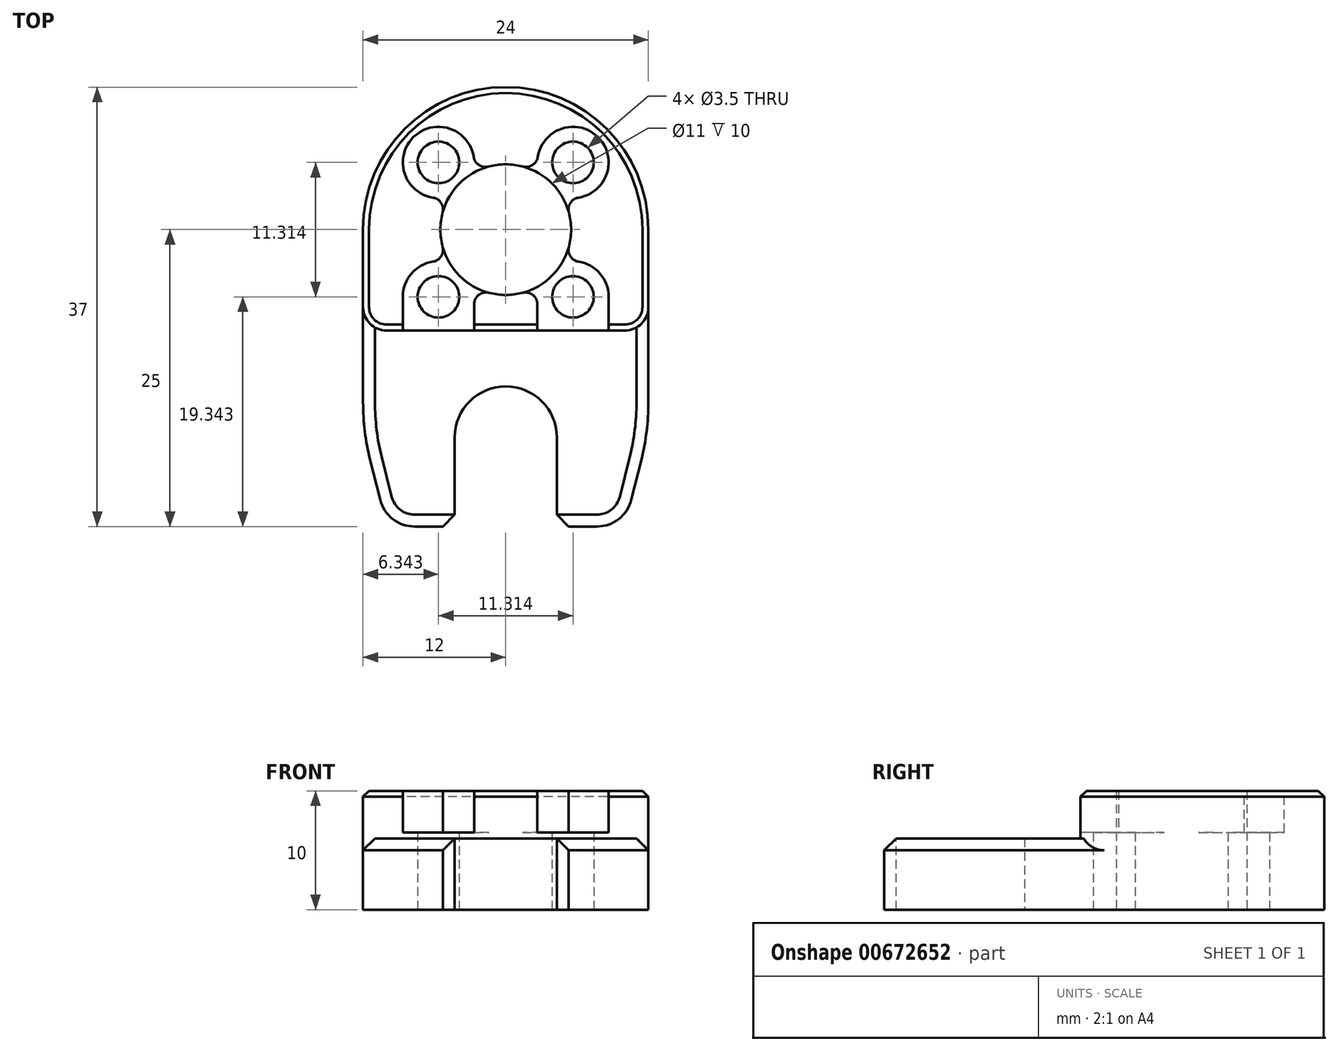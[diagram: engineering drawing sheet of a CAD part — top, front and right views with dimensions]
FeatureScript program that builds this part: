
annotation { "Feature Type Name" : "Feature", "Feature Type Description" : "" }
export const myFeature = defineFeature(function(context is Context, id is Id, definition is map)
    precondition{}
    {
        {
            var Q0;
            Q0=qCreatedBy(makeId("Top.planeOp"),FACE);
            var sketch = newSketch(context, id + "F0", { "sketchPlane" : qUnion([Q0])});
            skCircle(sketch, "E0", {"center": v(0, 0) * mm, "radius": 5.5 * mm});
            skLineSegment(sketch, "E1", {"start": v(0, 0) * mm, "end": v(0, 8) * mm, "construction": true});
            skCircle(sketch, "E2", {"center": v(0, 8) * mm, "radius": 1.75 * mm});
            skCircle(sketch, "E3.1.0", {"center": v(-8, 0) * mm, "radius": 1.75 * mm});
            skCircle(sketch, "E3.2.0", {"center": v(0, -8) * mm, "radius": 1.75 * mm});
            skCircle(sketch, "E3.3.0", {"center": v(8, 0) * mm, "radius": 1.75 * mm});
            skLineSegment(sketch, "E4", {"start": v(0, 0) * mm, "end": v(8, 0) * mm, "construction": true});
            skArc(sketch, "E5", {"start": v(8.49, -8.49) * mm, "mid": v(8.49, 8.49) * mm, "end": v(-8.49, 8.49) * mm});
            skLineSegment(sketch, "E6", {"start": v(0, 0) * mm, "end": v(-17.68, -17.68) * mm, "construction": true});
            skLineSegment(sketch, "E7", {"start": v(-17.68, -17.68) * mm, "end": v(-12.37, -12.37) * mm, "construction": true});
            skArc(sketch, "E8.0.startCap", {"start": v(-14.64, -20.72) * mm, "mid": v(-20.72, -20.72) * mm, "end": v(-20.72, -14.64) * mm, "construction": true});
            skArc(sketch, "E8.0.endCap", {"start": v(-15.41, -9.33) * mm, "mid": v(-9.33, -9.33) * mm, "end": v(-9.33, -15.41) * mm});
            skLineSegment(sketch, "E8.0.left", {"start": v(-20.72, -14.64) * mm, "end": v(-15.41, -9.33) * mm});
            skLineSegment(sketch, "E8.0.right", {"start": v(-14.64, -20.72) * mm, "end": v(-9.33, -15.41) * mm});
            skLineSegment(sketch, "E9", {"start": v(8.49, -8.49) * mm, "end": v(-9.2, -26.16) * mm});
            skLineSegment(sketch, "E10", {"start": v(-8.49, 8.49) * mm, "end": v(-26.16, -9.2) * mm});
            skLineSegment(sketch, "E11", {"start": v(-14.64, -20.72) * mm, "end": v(-9.2, -26.16) * mm});
            skLineSegment(sketch, "E12", {"start": v(-20.72, -14.64) * mm, "end": v(-26.16, -9.2) * mm});
            skSolve(sketch);
        }
        {
            var Q0;
            Q0 = qSketchRegion(id + "F0", true);
            extrude(context, id + "F1", {"entities" : qUnion([Q0]), "depth" : 10 * mm, "offsetDistance" : 25 * mm});
        }
        {
            var Q0;
            Q0=makeQuery(id+"F1.opExtrude","SWEPT_EDGE",EDGE,{"disambiguationData":[OSD([sQuery(id+"F0.wireOp",EDGE,"E10"),sQuery(id+"F0.wireOp",EDGE,"E12")])]});
            chamfer(context, id + "F2", {"entities" : qUnion([Q0]), "chamferType" : ChamferType.TWO_OFFSETS, "width1" : 2 * mm, "oppositeDirection" : false, "width2" : 8 * mm, "tangentPropagation" : true});
        }
        {
            var Q0;
            Q0=makeQuery(id+"F1.opExtrude","SWEPT_EDGE",EDGE,{"disambiguationData":[OSD([sQuery(id+"F0.wireOp",EDGE,"E9"),sQuery(id+"F0.wireOp",EDGE,"E11")])]});
            chamfer(context, id + "F3", {"entities" : qUnion([Q0]), "chamferType" : ChamferType.TWO_OFFSETS, "width1" : 8 * mm, "oppositeDirection" : false, "width2" : 2 * mm, "tangentPropagation" : true});
        }
        {
            var Q0;
            Q0=makeQuery(id+"F1.opExtrude","SWEPT_FACE",FACE,{"disambiguationData":[OSD([sQuery(id+"F0.wireOp",EDGE,"E8.0.left")])]});
            cPlane(context, id + "F4", {"entities" : qUnion([Q0]), "cplaneType" : CPlaneType.OFFSET, "offset" : 5.05 * mm, "width" : 150 * mm, "height" : 150 * mm});
        }
        {
            var Q0;
            Q0=qCreatedBy(id+"F4.planeOp",FACE);
            var sketch = newSketch(context, id + "F5", { "sketchPlane" : qUnion([Q0])});
            skLineSegment(sketch, "E13", {"start": v(0, 0) * mm, "end": v(-8.5, 0) * mm, "construction": true});
            skLineSegment(sketch, "E14", {"start": v(-8.5, 0) * mm, "end": v(-8.5, 6) * mm, "construction": true});
            skLineSegment(sketch, "E15.bottom", {"start": v(-8.5, 6) * mm, "end": v(-28.5, 6) * mm});
            skLineSegment(sketch, "E15.top", {"start": v(-8.5, 14) * mm, "end": v(-28.5, 14) * mm});
            skLineSegment(sketch, "E15.left", {"start": v(-8.5, 6) * mm, "end": v(-8.5, 14) * mm});
            skLineSegment(sketch, "E15.right", {"start": v(-28.5, 6) * mm, "end": v(-28.5, 14) * mm});
            skSolve(sketch);
        }
        {
            var Q0;
            Q0 = qSketchRegion(id + "F5", true);
            extrude(context, id + "F6", {"entities" : qUnion([Q0]), "operationType" : NewBodyOperationType.REMOVE, "endBound" : BoundingType.SYMMETRIC, "oppositeDirection" : true, "depth" : 30 * mm, "offsetDistance" : 25 * mm});
        }
        {
            var Q0;
            Q0=makeQuery(id+"F1.opExtrude","CAP_FACE",FACE,{"disambiguationData":[OSD([sQuery(id+"F0.wireOp",EDGE,"E0"),sQuery(id+"F0.wireOp",EDGE,"E2"),sQuery(id+"F0.wireOp",EDGE,"E3.1.0"),sQuery(id+"F0.wireOp",EDGE,"E3.2.0"),sQuery(id+"F0.wireOp",EDGE,"E3.3.0"),sQuery(id+"F0.wireOp",EDGE,"E5"),sQuery(id+"F0.wireOp",EDGE,"E8.0.endCap"),sQuery(id+"F0.wireOp",EDGE,"E8.0.left"),sQuery(id+"F0.wireOp",EDGE,"E8.0.right"),sQuery(id+"F0.wireOp",EDGE,"E9"),sQuery(id+"F0.wireOp",EDGE,"E10"),sQuery(id+"F0.wireOp",EDGE,"E11"),sQuery(id+"F0.wireOp",EDGE,"E12")])],"isStart":false});
            var sketch = newSketch(context, id + "F7", { "sketchPlane" : qUnion([Q0])});
            skArc(sketch, "E16", {"start": v(-5.88, -2.12) * mm, "mid": v(-5.88, 2.12) * mm, "end": v(-10.12, 2.12) * mm});
            skArc(sketch, "E17", {"start": v(2.12, -10.12) * mm, "mid": v(2.12, -5.88) * mm, "end": v(-2.12, -5.88) * mm});
            skCircle(sketch, "E18", {"center": v(8, 0) * mm, "radius": 3 * mm});
            skCircle(sketch, "E19", {"center": v(0, 8) * mm, "radius": 3 * mm});
            skLineSegment(sketch, "E20", {"start": v(-8, 0) * mm, "end": v(-10.01, -2.01) * mm, "construction": true});
            skLineSegment(sketch, "E21", {"start": v(0, -8) * mm, "end": v(-2.01, -10.01) * mm, "construction": true});
            skLineSegment(sketch, "E22.0", {"start": v(-10.12, 2.12) * mm, "end": v(-12.13, 0.11) * mm});
            skLineSegment(sketch, "E23.MirrorCS", {"start": v(-5.88, -2.12) * mm, "end": v(-7.89, -4.13) * mm});
            skLineSegment(sketch, "E24", {"start": v(-12.13, 0.11) * mm, "end": v(-7.89, -4.13) * mm});
            skLineSegment(sketch, "E25.0", {"start": v(-2.12, -5.88) * mm, "end": v(-4.13, -7.89) * mm});
            skLineSegment(sketch, "E26.MirrorCS", {"start": v(2.12, -10.12) * mm, "end": v(0.11, -12.13) * mm});
            skLineSegment(sketch, "E27", {"start": v(-4.13, -7.89) * mm, "end": v(0.11, -12.13) * mm});
            skSolve(sketch);
        }
        {
            var Q0;
            Q0 = qSketchRegion(id + "F7", true);
            extrude(context, id + "F8", {"entities" : qUnion([Q0]), "operationType" : NewBodyOperationType.REMOVE, "oppositeDirection" : true, "depth" : 3.5 * mm, "offsetDistance" : 25 * mm});
        }
        {
            var Q0;
            Q0=makeQuery(id+"F8.boolean.opBoolean","INTERSECT",EDGE,{"disambiguationData":[OD(0.0)],"derivedFrom":[makeQuery(id+"F1.opExtrude","SWEPT_FACE",FACE,{"disambiguationData":[OSD([sQuery(id+"F0.wireOp",EDGE,"E0")])]}),makeQuery(id+"F8.opExtrude","SWEPT_FACE",FACE,{"disambiguationData":[OSD([sQuery(id+"F7.wireOp",EDGE,"E16")])]})]});
            var Q1;
            Q1=makeQuery(id+"F8.boolean.opBoolean","INTERSECT",EDGE,{"disambiguationData":[OD(1.0)],"derivedFrom":[makeQuery(id+"F1.opExtrude","SWEPT_FACE",FACE,{"disambiguationData":[OSD([sQuery(id+"F0.wireOp",EDGE,"E0")])]}),makeQuery(id+"F8.opExtrude","SWEPT_FACE",FACE,{"disambiguationData":[OSD([sQuery(id+"F7.wireOp",EDGE,"E16")])]})]});
            var Q2;
            Q2=makeQuery(id+"F8.boolean.opBoolean","INTERSECT",EDGE,{"disambiguationData":[OD(0.0)],"derivedFrom":[makeQuery(id+"F1.opExtrude","SWEPT_FACE",FACE,{"disambiguationData":[OSD([sQuery(id+"F0.wireOp",EDGE,"E0")])]}),makeQuery(id+"F8.opExtrude","SWEPT_FACE",FACE,{"disambiguationData":[OSD([sQuery(id+"F7.wireOp",EDGE,"E17")])]})]});
            var Q3;
            Q3=makeQuery(id+"F8.boolean.opBoolean","INTERSECT",EDGE,{"disambiguationData":[OD(1.0)],"derivedFrom":[makeQuery(id+"F1.opExtrude","SWEPT_FACE",FACE,{"disambiguationData":[OSD([sQuery(id+"F0.wireOp",EDGE,"E0")])]}),makeQuery(id+"F8.opExtrude","SWEPT_FACE",FACE,{"disambiguationData":[OSD([sQuery(id+"F7.wireOp",EDGE,"E17")])]})]});
            var Q4;
            Q4=makeQuery(id+"F8.boolean.opBoolean","INTERSECT",EDGE,{"disambiguationData":[OD(0.0)],"derivedFrom":[makeQuery(id+"F1.opExtrude","SWEPT_FACE",FACE,{"disambiguationData":[OSD([sQuery(id+"F0.wireOp",EDGE,"E0")])]}),makeQuery(id+"F8.opExtrude","SWEPT_FACE",FACE,{"disambiguationData":[OSD([sQuery(id+"F7.wireOp",EDGE,"E18")])]})]});
            var Q5;
            Q5=makeQuery(id+"F8.boolean.opBoolean","INTERSECT",EDGE,{"disambiguationData":[OD(1.0)],"derivedFrom":[makeQuery(id+"F1.opExtrude","SWEPT_FACE",FACE,{"disambiguationData":[OSD([sQuery(id+"F0.wireOp",EDGE,"E0")])]}),makeQuery(id+"F8.opExtrude","SWEPT_FACE",FACE,{"disambiguationData":[OSD([sQuery(id+"F7.wireOp",EDGE,"E18")])]})]});
            var Q6;
            Q6=makeQuery(id+"F8.boolean.opBoolean","INTERSECT",EDGE,{"disambiguationData":[OD(1.0)],"derivedFrom":[makeQuery(id+"F1.opExtrude","SWEPT_FACE",FACE,{"disambiguationData":[OSD([sQuery(id+"F0.wireOp",EDGE,"E0")])]}),makeQuery(id+"F8.opExtrude","SWEPT_FACE",FACE,{"disambiguationData":[OSD([sQuery(id+"F7.wireOp",EDGE,"E19")])]})]});
            var Q7;
            Q7=makeQuery(id+"F8.boolean.opBoolean","INTERSECT",EDGE,{"disambiguationData":[OD(0.0)],"derivedFrom":[makeQuery(id+"F1.opExtrude","SWEPT_FACE",FACE,{"disambiguationData":[OSD([sQuery(id+"F0.wireOp",EDGE,"E0")])]}),makeQuery(id+"F8.opExtrude","SWEPT_FACE",FACE,{"disambiguationData":[OSD([sQuery(id+"F7.wireOp",EDGE,"E19")])]})]});
            fillet(context, id + "F9", {"entities" : qUnion([Q0, Q1, Q2, Q3, Q4, Q5, Q6, Q7]), "radius" : 1 * mm, "tangentPropagation" : true, "allowEdgeOverflow" : false});
        }
        {
            var Q0;
            Q0=makeQuery(id+"F6.boolean.opBoolean","INTERSECT",EDGE,{"derivedFrom":[makeQuery(id+"F1.opExtrude","SWEPT_FACE",FACE,{"disambiguationData":[OSD([sQuery(id+"F0.wireOp",EDGE,"E9")])]}),makeQuery(id+"F6.opExtrude","SWEPT_FACE",FACE,{"disambiguationData":[OSD([sQuery(id+"F5.wireOp",EDGE,"E15.left")])]})]});
            var Q1;
            Q1=makeQuery(id+"F6.boolean.opBoolean","INTERSECT",EDGE,{"derivedFrom":[makeQuery(id+"F1.opExtrude","SWEPT_FACE",FACE,{"disambiguationData":[OSD([sQuery(id+"F0.wireOp",EDGE,"E10")])]}),makeQuery(id+"F6.opExtrude","SWEPT_FACE",FACE,{"disambiguationData":[OSD([sQuery(id+"F5.wireOp",EDGE,"E15.left")])]})]});
            fillet(context, id + "F10", {"entities" : qUnion([Q0, Q1]), "radius" : 2 * mm, "tangentPropagation" : true, "allowEdgeOverflow" : false});
        }
        {
            var Q0;
            Q0=makeQuery(id+"F6.boolean.opBoolean","INTERSECT",EDGE,{"derivedFrom":[makeQuery(id+"F1.opExtrude","CAP_FACE",FACE,{"disambiguationData":[OSD([sQuery(id+"F0.wireOp",EDGE,"E0"),sQuery(id+"F0.wireOp",EDGE,"E2"),sQuery(id+"F0.wireOp",EDGE,"E3.1.0"),sQuery(id+"F0.wireOp",EDGE,"E3.2.0"),sQuery(id+"F0.wireOp",EDGE,"E3.3.0"),sQuery(id+"F0.wireOp",EDGE,"E5"),sQuery(id+"F0.wireOp",EDGE,"E8.0.endCap"),sQuery(id+"F0.wireOp",EDGE,"E8.0.left"),sQuery(id+"F0.wireOp",EDGE,"E8.0.right"),sQuery(id+"F0.wireOp",EDGE,"E9"),sQuery(id+"F0.wireOp",EDGE,"E10"),sQuery(id+"F0.wireOp",EDGE,"E11"),sQuery(id+"F0.wireOp",EDGE,"E12")])],"isStart":false}),makeQuery(id+"F6.opExtrude","SWEPT_FACE",FACE,{"disambiguationData":[OSD([sQuery(id+"F5.wireOp",EDGE,"E15.left")])]})]});
            var Q1;
            {var subQ0=sQuery(id+"F0.wireOp",EDGE,"E9");Q1=makeQuery(id+"F10.opFillet","BLEND_EDGE",EDGE,{"blendedFrom":[makeQuery(id+"F6.boolean.opBoolean","INTERSECT",EDGE,{"derivedFrom":[makeQuery(id+"F1.opExtrude","SWEPT_FACE",FACE,{"disambiguationData":[OSD([subQ0])]}),makeQuery(id+"F6.opExtrude","SWEPT_FACE",FACE,{"disambiguationData":[OSD([sQuery(id+"F5.wireOp",EDGE,"E15.left")])]})]}),makeQuery(id+"F1.opExtrude","CAP_FACE",FACE,{"disambiguationData":[OSD([sQuery(id+"F0.wireOp",EDGE,"E0"),sQuery(id+"F0.wireOp",EDGE,"E2"),sQuery(id+"F0.wireOp",EDGE,"E3.1.0"),sQuery(id+"F0.wireOp",EDGE,"E3.2.0"),sQuery(id+"F0.wireOp",EDGE,"E3.3.0"),sQuery(id+"F0.wireOp",EDGE,"E5"),sQuery(id+"F0.wireOp",EDGE,"E8.0.endCap"),sQuery(id+"F0.wireOp",EDGE,"E8.0.left"),sQuery(id+"F0.wireOp",EDGE,"E8.0.right"),subQ0,sQuery(id+"F0.wireOp",EDGE,"E10"),sQuery(id+"F0.wireOp",EDGE,"E11"),sQuery(id+"F0.wireOp",EDGE,"E12")])],"isStart":false})],"blendedInto":[makeQuery(id+"F1.opExtrude","CAP_FACE",FACE,{"disambiguationData":[OSD([sQuery(id+"F0.wireOp",EDGE,"E0"),sQuery(id+"F0.wireOp",EDGE,"E2"),sQuery(id+"F0.wireOp",EDGE,"E3.1.0"),sQuery(id+"F0.wireOp",EDGE,"E3.2.0"),sQuery(id+"F0.wireOp",EDGE,"E3.3.0"),sQuery(id+"F0.wireOp",EDGE,"E5"),sQuery(id+"F0.wireOp",EDGE,"E8.0.endCap"),sQuery(id+"F0.wireOp",EDGE,"E8.0.left"),sQuery(id+"F0.wireOp",EDGE,"E8.0.right"),subQ0,sQuery(id+"F0.wireOp",EDGE,"E10"),sQuery(id+"F0.wireOp",EDGE,"E11"),sQuery(id+"F0.wireOp",EDGE,"E12")])],"isStart":false})]});}
            var Q2;
            {var subQ0=sQuery(id+"F0.wireOp",EDGE,"E10");Q2=makeQuery(id+"F10.opFillet","BLEND_EDGE",EDGE,{"blendedFrom":[makeQuery(id+"F6.boolean.opBoolean","INTERSECT",EDGE,{"derivedFrom":[makeQuery(id+"F1.opExtrude","SWEPT_FACE",FACE,{"disambiguationData":[OSD([subQ0])]}),makeQuery(id+"F6.opExtrude","SWEPT_FACE",FACE,{"disambiguationData":[OSD([sQuery(id+"F5.wireOp",EDGE,"E15.left")])]})]}),makeQuery(id+"F1.opExtrude","CAP_FACE",FACE,{"disambiguationData":[OSD([sQuery(id+"F0.wireOp",EDGE,"E0"),sQuery(id+"F0.wireOp",EDGE,"E2"),sQuery(id+"F0.wireOp",EDGE,"E3.1.0"),sQuery(id+"F0.wireOp",EDGE,"E3.2.0"),sQuery(id+"F0.wireOp",EDGE,"E3.3.0"),sQuery(id+"F0.wireOp",EDGE,"E5"),sQuery(id+"F0.wireOp",EDGE,"E8.0.endCap"),sQuery(id+"F0.wireOp",EDGE,"E8.0.left"),sQuery(id+"F0.wireOp",EDGE,"E8.0.right"),sQuery(id+"F0.wireOp",EDGE,"E9"),subQ0,sQuery(id+"F0.wireOp",EDGE,"E11"),sQuery(id+"F0.wireOp",EDGE,"E12")])],"isStart":false})],"blendedInto":[makeQuery(id+"F1.opExtrude","CAP_FACE",FACE,{"disambiguationData":[OSD([sQuery(id+"F0.wireOp",EDGE,"E0"),sQuery(id+"F0.wireOp",EDGE,"E2"),sQuery(id+"F0.wireOp",EDGE,"E3.1.0"),sQuery(id+"F0.wireOp",EDGE,"E3.2.0"),sQuery(id+"F0.wireOp",EDGE,"E3.3.0"),sQuery(id+"F0.wireOp",EDGE,"E5"),sQuery(id+"F0.wireOp",EDGE,"E8.0.endCap"),sQuery(id+"F0.wireOp",EDGE,"E8.0.left"),sQuery(id+"F0.wireOp",EDGE,"E8.0.right"),sQuery(id+"F0.wireOp",EDGE,"E9"),subQ0,sQuery(id+"F0.wireOp",EDGE,"E11"),sQuery(id+"F0.wireOp",EDGE,"E12")])],"isStart":false})]});}
            var Q3;
            Q3=makeQuery(id+"F1.opExtrude","CAP_EDGE",EDGE,{"disambiguationData":[OSD([sQuery(id+"F0.wireOp",EDGE,"E9")])],"isStart":false});
            var Q4;
            Q4=makeQuery(id+"F1.opExtrude","CAP_EDGE",EDGE,{"disambiguationData":[OSD([sQuery(id+"F0.wireOp",EDGE,"E5")])],"isStart":false});
            var Q5;
            Q5=makeQuery(id+"F1.opExtrude","CAP_EDGE",EDGE,{"disambiguationData":[OSD([sQuery(id+"F0.wireOp",EDGE,"E10")])],"isStart":false});
            chamfer(context, id + "F11", {"entities" : qUnion([Q0, Q1, Q2, Q3, Q4, Q5]), "width" : 0.5 * mm});
        }
        {
            var Q0;
            Q0=makeQuery(id+"F1.opExtrude","SWEPT_EDGE",EDGE,{"disambiguationData":[OSD([sQuery(id+"F0.wireOp",EDGE,"E8.0.left"),sQuery(id+"F0.wireOp",EDGE,"E12")])]});
            var Q1;
            Q1=makeQuery(id+"F1.opExtrude","SWEPT_EDGE",EDGE,{"disambiguationData":[OSD([sQuery(id+"F0.wireOp",EDGE,"E8.0.right"),sQuery(id+"F0.wireOp",EDGE,"E11")])]});
            chamfer(context, id + "F12", {"entities" : qUnion([Q0, Q1]), "width" : 1 * mm, "tangentPropagation" : true});
        }
        {
            var Q0;
            {var subQ0=sQuery(id+"F0.wireOp",EDGE,"E11");Q0=makeQuery(id+"F3.opChamfer","BLEND_EDGE",EDGE,{"blendedFrom":[makeQuery(id+"F1.opExtrude","SWEPT_EDGE",EDGE,{"disambiguationData":[OSD([sQuery(id+"F0.wireOp",EDGE,"E9"),subQ0])]}),makeQuery(id+"F1.opExtrude","SWEPT_FACE",FACE,{"disambiguationData":[OSD([subQ0])]})],"blendedInto":[makeQuery(id+"F1.opExtrude","SWEPT_FACE",FACE,{"disambiguationData":[OSD([subQ0])]})]});}
            var Q1;
            {var subQ0=sQuery(id+"F0.wireOp",EDGE,"E12");Q1=makeQuery(id+"F2.opChamfer","BLEND_EDGE",EDGE,{"blendedFrom":[makeQuery(id+"F1.opExtrude","SWEPT_EDGE",EDGE,{"disambiguationData":[OSD([sQuery(id+"F0.wireOp",EDGE,"E10"),subQ0])]}),makeQuery(id+"F1.opExtrude","SWEPT_FACE",FACE,{"disambiguationData":[OSD([subQ0])]})],"blendedInto":[makeQuery(id+"F1.opExtrude","SWEPT_FACE",FACE,{"disambiguationData":[OSD([subQ0])]})]});}
            fillet(context, id + "F13", {"entities" : qUnion([Q0, Q1]), "radius" : 3 * mm, "tangentPropagation" : true, "allowEdgeOverflow" : false});
        }
        {
            var Q0;
            {var subQ0=sQuery(id+"F0.wireOp",EDGE,"E9");Q0=makeQuery(id+"F3.opChamfer","BLEND_EDGE",EDGE,{"blendedFrom":[makeQuery(id+"F1.opExtrude","SWEPT_EDGE",EDGE,{"disambiguationData":[OSD([subQ0,sQuery(id+"F0.wireOp",EDGE,"E11")])]}),makeQuery(id+"F1.opExtrude","SWEPT_FACE",FACE,{"disambiguationData":[OSD([subQ0])]})],"blendedInto":[makeQuery(id+"F1.opExtrude","SWEPT_FACE",FACE,{"disambiguationData":[OSD([subQ0])]})]});}
            var Q1;
            {var subQ0=sQuery(id+"F0.wireOp",EDGE,"E10");Q1=makeQuery(id+"F2.opChamfer","BLEND_EDGE",EDGE,{"blendedFrom":[makeQuery(id+"F1.opExtrude","SWEPT_EDGE",EDGE,{"disambiguationData":[OSD([subQ0,sQuery(id+"F0.wireOp",EDGE,"E12")])]}),makeQuery(id+"F1.opExtrude","SWEPT_FACE",FACE,{"disambiguationData":[OSD([subQ0])]})],"blendedInto":[makeQuery(id+"F1.opExtrude","SWEPT_FACE",FACE,{"disambiguationData":[OSD([subQ0])]})]});}
            fillet(context, id + "F14", {"entities" : qUnion([Q0, Q1]), "radius" : 20 * mm, "tangentPropagation" : true, "allowEdgeOverflow" : false});
        }
        {
            var Q0;
            Q0=makeQuery(id+"F6.boolean.opBoolean","INTERSECT",EDGE,{"derivedFrom":[makeQuery(id+"F1.opExtrude","SWEPT_FACE",FACE,{"disambiguationData":[OSD([sQuery(id+"F0.wireOp",EDGE,"E11")])]}),makeQuery(id+"F6.opExtrude","SWEPT_FACE",FACE,{"disambiguationData":[OSD([sQuery(id+"F5.wireOp",EDGE,"E15.bottom")])]})]});
            var Q1;
            {var subQ0=sQuery(id+"F0.wireOp",EDGE,"E11");Q1=makeQuery(id+"F13.opFillet","BLEND_EDGE",EDGE,{"blendedFrom":[makeQuery(id+"F3.opChamfer","BLEND_EDGE",EDGE,{"blendedFrom":[makeQuery(id+"F1.opExtrude","SWEPT_EDGE",EDGE,{"disambiguationData":[OSD([sQuery(id+"F0.wireOp",EDGE,"E9"),subQ0])]}),makeQuery(id+"F1.opExtrude","SWEPT_FACE",FACE,{"disambiguationData":[OSD([subQ0])]})],"blendedInto":[makeQuery(id+"F1.opExtrude","SWEPT_FACE",FACE,{"disambiguationData":[OSD([subQ0])]})]}),makeQuery(id+"F6.boolean.opBoolean","COPY",FACE,{"derivedFrom":makeQuery(id+"F6.opExtrude","SWEPT_FACE",FACE,{"disambiguationData":[OSD([sQuery(id+"F5.wireOp",EDGE,"E15.bottom")])]})})],"blendedInto":[makeQuery(id+"F6.boolean.opBoolean","COPY",FACE,{"derivedFrom":makeQuery(id+"F6.opExtrude","SWEPT_FACE",FACE,{"disambiguationData":[OSD([sQuery(id+"F5.wireOp",EDGE,"E15.bottom")])]})})]});}
            var Q2;
            Q2=makeQuery(id+"F6.boolean.opBoolean","INTERSECT",EDGE,{"derivedFrom":[makeQuery(id+"F3.opChamfer","BLEND_FACE",FACE,{"disambiguationData":[OSD([sQuery(id+"F0.wireOp",EDGE,"E9"),sQuery(id+"F0.wireOp",EDGE,"E11")])]}),makeQuery(id+"F6.opExtrude","SWEPT_FACE",FACE,{"disambiguationData":[OSD([sQuery(id+"F5.wireOp",EDGE,"E15.bottom")])]})]});
            var Q3;
            {var subQ0=sQuery(id+"F0.wireOp",EDGE,"E9");Q3=makeQuery(id+"F14.opFillet","BLEND_EDGE",EDGE,{"blendedFrom":[makeQuery(id+"F3.opChamfer","BLEND_EDGE",EDGE,{"blendedFrom":[makeQuery(id+"F1.opExtrude","SWEPT_EDGE",EDGE,{"disambiguationData":[OSD([subQ0,sQuery(id+"F0.wireOp",EDGE,"E11")])]}),makeQuery(id+"F1.opExtrude","SWEPT_FACE",FACE,{"disambiguationData":[OSD([subQ0])]})],"blendedInto":[makeQuery(id+"F1.opExtrude","SWEPT_FACE",FACE,{"disambiguationData":[OSD([subQ0])]})]}),makeQuery(id+"F6.boolean.opBoolean","COPY",FACE,{"derivedFrom":makeQuery(id+"F6.opExtrude","SWEPT_FACE",FACE,{"disambiguationData":[OSD([sQuery(id+"F5.wireOp",EDGE,"E15.bottom")])]})})],"blendedInto":[makeQuery(id+"F6.boolean.opBoolean","COPY",FACE,{"derivedFrom":makeQuery(id+"F6.opExtrude","SWEPT_FACE",FACE,{"disambiguationData":[OSD([sQuery(id+"F5.wireOp",EDGE,"E15.bottom")])]})})]});}
            var Q4;
            Q4=makeQuery(id+"F6.boolean.opBoolean","INTERSECT",EDGE,{"derivedFrom":[makeQuery(id+"F1.opExtrude","SWEPT_FACE",FACE,{"disambiguationData":[OSD([sQuery(id+"F0.wireOp",EDGE,"E9")])]}),makeQuery(id+"F6.opExtrude","SWEPT_FACE",FACE,{"disambiguationData":[OSD([sQuery(id+"F5.wireOp",EDGE,"E15.bottom")])]})]});
            var Q5;
            Q5=makeQuery(id+"F6.boolean.opBoolean","INTERSECT",EDGE,{"derivedFrom":[makeQuery(id+"F1.opExtrude","SWEPT_FACE",FACE,{"disambiguationData":[OSD([sQuery(id+"F0.wireOp",EDGE,"E12")])]}),makeQuery(id+"F6.opExtrude","SWEPT_FACE",FACE,{"disambiguationData":[OSD([sQuery(id+"F5.wireOp",EDGE,"E15.bottom")])]})]});
            var Q6;
            {var subQ0=sQuery(id+"F0.wireOp",EDGE,"E12");Q6=makeQuery(id+"F13.opFillet","BLEND_EDGE",EDGE,{"blendedFrom":[makeQuery(id+"F2.opChamfer","BLEND_EDGE",EDGE,{"blendedFrom":[makeQuery(id+"F1.opExtrude","SWEPT_EDGE",EDGE,{"disambiguationData":[OSD([sQuery(id+"F0.wireOp",EDGE,"E10"),subQ0])]}),makeQuery(id+"F1.opExtrude","SWEPT_FACE",FACE,{"disambiguationData":[OSD([subQ0])]})],"blendedInto":[makeQuery(id+"F1.opExtrude","SWEPT_FACE",FACE,{"disambiguationData":[OSD([subQ0])]})]}),makeQuery(id+"F6.boolean.opBoolean","COPY",FACE,{"derivedFrom":makeQuery(id+"F6.opExtrude","SWEPT_FACE",FACE,{"disambiguationData":[OSD([sQuery(id+"F5.wireOp",EDGE,"E15.bottom")])]})})],"blendedInto":[makeQuery(id+"F6.boolean.opBoolean","COPY",FACE,{"derivedFrom":makeQuery(id+"F6.opExtrude","SWEPT_FACE",FACE,{"disambiguationData":[OSD([sQuery(id+"F5.wireOp",EDGE,"E15.bottom")])]})})]});}
            var Q7;
            Q7=makeQuery(id+"F6.boolean.opBoolean","INTERSECT",EDGE,{"derivedFrom":[makeQuery(id+"F2.opChamfer","BLEND_FACE",FACE,{"disambiguationData":[OSD([sQuery(id+"F0.wireOp",EDGE,"E10"),sQuery(id+"F0.wireOp",EDGE,"E12")])]}),makeQuery(id+"F6.opExtrude","SWEPT_FACE",FACE,{"disambiguationData":[OSD([sQuery(id+"F5.wireOp",EDGE,"E15.bottom")])]})]});
            chamfer(context, id + "F15", {"entities" : qUnion([Q0, Q1, Q2, Q3, Q4, Q5, Q6, Q7]), "width" : 1 * mm, "tangentPropagation" : true});
        }
        {
            var Q0;
            Q0=qCreatedBy(makeId("Front.planeOp"),FACE);
            var sketch = newSketch(context, id + "F16", { "sketchPlane" : qUnion([Q0])});
            skLineSegment(sketch, "E28", {"start": v(0, 0) * mm, "end": v(0, 25) * mm, "construction": true});
            skSolve(sketch);
        }
        {
            var Q0;
            Q0=makeQuery(id+"F1.opExtrude","SWEPT_BODY",BODY,{"disambiguationData":[OSD([sQuery(id+"F0.wireOp",EDGE,"E0"),sQuery(id+"F0.wireOp",EDGE,"E2"),sQuery(id+"F0.wireOp",EDGE,"E3.1.0"),sQuery(id+"F0.wireOp",EDGE,"E3.2.0"),sQuery(id+"F0.wireOp",EDGE,"E3.3.0"),sQuery(id+"F0.wireOp",EDGE,"E5"),sQuery(id+"F0.wireOp",EDGE,"E8.0.endCap"),sQuery(id+"F0.wireOp",EDGE,"E8.0.left"),sQuery(id+"F0.wireOp",EDGE,"E8.0.right"),sQuery(id+"F0.wireOp",EDGE,"E9"),sQuery(id+"F0.wireOp",EDGE,"E10"),sQuery(id+"F0.wireOp",EDGE,"E11"),sQuery(id+"F0.wireOp",EDGE,"E12")])]});
            var Q1;
            Q1=sQuery(id+"F16.wireOp",EDGE,"E28");
            var Q2;
            Q2=sQuery(id+"F16.wireOp",EDGE,"E28");
            transform(context, id + "F17", {"entities" : qUnion([Q0]), "transformType" : TransformType.ROTATION, "transformAxis" : qUnion([Q2]), "angle" : 45 * degree, "makeCopy" : false});
        }
    });
